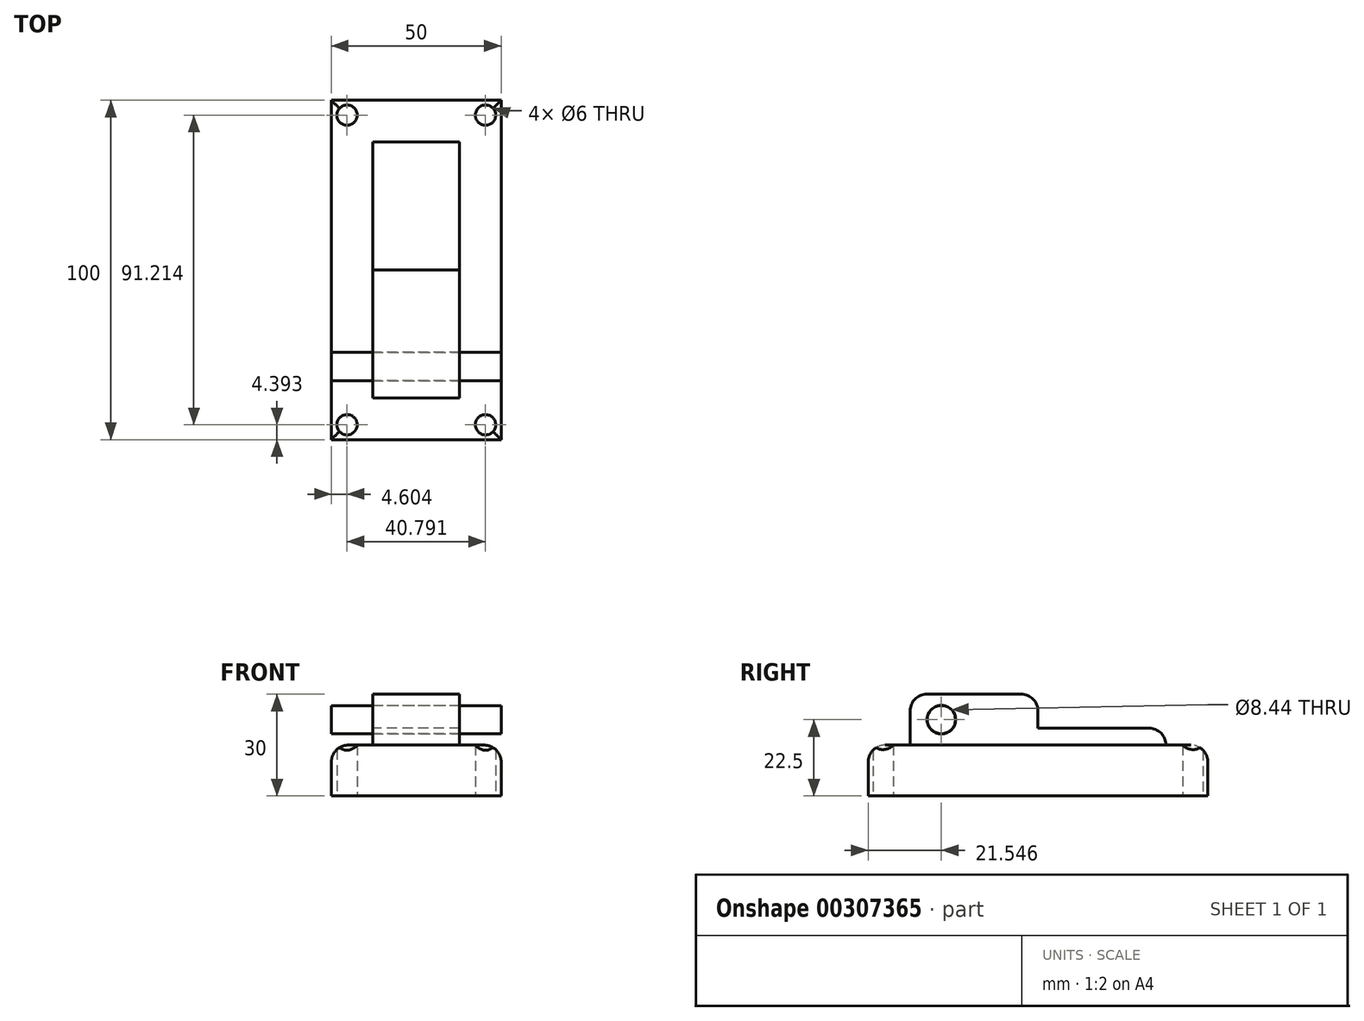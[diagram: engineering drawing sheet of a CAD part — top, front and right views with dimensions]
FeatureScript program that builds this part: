
annotation { "Feature Type Name" : "Feature", "Feature Type Description" : "" }
export const myFeature = defineFeature(function(context is Context, id is Id, definition is map)
    precondition{}
    {
        {
            var Q0;
            Q0=qCreatedBy(makeId("Top.planeOp"),FACE);
            var sketch = newSketch(context, id + "F0", { "sketchPlane" : qUnion([Q0])});
            skLineSegment(sketch, "E0.bottom", {"start": v(25, 50) * mm, "end": v(-25, 50) * mm});
            skLineSegment(sketch, "E0.top", {"start": v(25, -50) * mm, "end": v(-25, -50) * mm});
            skLineSegment(sketch, "E0.left", {"start": v(25, 50) * mm, "end": v(25, -50) * mm});
            skLineSegment(sketch, "E0.right", {"start": v(-25, 50) * mm, "end": v(-25, -50) * mm});
            skPoint(sketch, "E0.middle", {"position": v(0, 0) * mm});
            skLineSegment(sketch, "E1.bottom", {"start": v(20.4, 45.6) * mm, "end": v(-20.4, 45.6) * mm, "construction": true});
            skLineSegment(sketch, "E1.top", {"start": v(20.4, -45.6) * mm, "end": v(-20.4, -45.6) * mm, "construction": true});
            skLineSegment(sketch, "E1.left", {"start": v(20.4, 45.6) * mm, "end": v(20.4, -45.6) * mm, "construction": true});
            skLineSegment(sketch, "E1.right", {"start": v(-20.4, 45.6) * mm, "end": v(-20.4, -45.6) * mm, "construction": true});
            skCircle(sketch, "E2", {"center": v(-20.4, 45.6) * mm, "radius": 3 * mm});
            skCircle(sketch, "E3", {"center": v(20.4, 45.6) * mm, "radius": 3 * mm});
            skCircle(sketch, "E4", {"center": v(-20.4, -45.6) * mm, "radius": 3 * mm});
            skCircle(sketch, "E5", {"center": v(20.4, -45.6) * mm, "radius": 3 * mm});
            skLineSegment(sketch, "E6.bottom", {"start": v(12.75, 37.68) * mm, "end": v(-12.75, 37.68) * mm});
            skLineSegment(sketch, "E6.top", {"start": v(12.75, -37.68) * mm, "end": v(-12.75, -37.68) * mm});
            skLineSegment(sketch, "E6.left", {"start": v(12.75, 37.68) * mm, "end": v(12.75, -37.68) * mm});
            skLineSegment(sketch, "E6.right", {"start": v(-12.75, 37.68) * mm, "end": v(-12.75, -37.68) * mm});
            skLineSegment(sketch, "E7.top", {"start": v(12.75, 0) * mm, "end": v(-12.75, 0) * mm});
            skLineSegment(sketch, "E7.left", {"start": v(12.75, 37.68) * mm, "end": v(12.75, 0) * mm});
            skLineSegment(sketch, "E7.right", {"start": v(-12.75, 37.68) * mm, "end": v(-12.75, 0) * mm});
            skSolve(sketch);
        }
        {
            var Q0;
            Q0=makeQuery(id+"F0.imprint","IMPRINT",FACE,{"disambiguationData":[TD([[makeQuery(id+"F0.imprint","IMPRINT",EDGE,{"derivedFrom":sQuery(id+"F0.wireOp",EDGE,"E0.bottom")}),1.0]])]});
            extrude(context, id + "F1", {"entities" : qUnion([Q0]), "depth" : 15 * mm});
        }
        {
            var Q0;
            Q0=makeQuery(id+"F0.imprint","IMPRINT",FACE,{"disambiguationData":[TD([[makeQuery(id+"F0.imprint","IMPRINT",EDGE,{"derivedFrom":sQuery(id+"F0.wireOp",EDGE,"E6.bottom")}),1.0]])]});
            extrude(context, id + "F2", {"entities" : qUnion([Q0]), "operationType" : NewBodyOperationType.ADD, "depth" : 20 * mm});
        }
        {
            var Q0;
            Q0=makeQuery(id+"F0.imprint","IMPRINT",FACE,{"disambiguationData":[TD([[makeQuery(id+"F0.imprint","IMPRINT",EDGE,{"derivedFrom":sQuery(id+"F0.wireOp",EDGE,"E6.top")}),-1.0]])]});
            extrude(context, id + "F3", {"entities" : qUnion([Q0]), "operationType" : NewBodyOperationType.ADD, "depth" : 30 * mm});
        }
        {
            var Q0;
            Q0=makeQuery(id+"F3.opExtrude","CAP_EDGE",EDGE,{"disambiguationData":[OSD([sQuery(id+"F0.wireOp",EDGE,"E7.top")])],"isStart":false});
            var Q1;
            Q1=makeQuery(id+"F2.opExtrude","CAP_EDGE",EDGE,{"disambiguationData":[OSD([sQuery(id+"F0.wireOp",EDGE,"E7.top")])],"isStart":false});
            var Q2;
            Q2=makeQuery(id+"F2.opExtrude","CAP_EDGE",EDGE,{"disambiguationData":[OSD([sQuery(id+"F0.wireOp",EDGE,"E6.bottom")])],"isStart":false});
            var Q3;
            Q3=makeQuery(id+"F1.opExtrude","CAP_EDGE",EDGE,{"disambiguationData":[OSD([sQuery(id+"F0.wireOp",EDGE,"E0.right")])],"isStart":false});
            var Q4;
            Q4=makeQuery(id+"F1.opExtrude","CAP_EDGE",EDGE,{"disambiguationData":[OSD([sQuery(id+"F0.wireOp",EDGE,"E0.top")])],"isStart":false});
            var Q5;
            Q5=makeQuery(id+"F1.opExtrude","CAP_EDGE",EDGE,{"disambiguationData":[OSD([sQuery(id+"F0.wireOp",EDGE,"E0.left")])],"isStart":false});
            var Q6;
            Q6=makeQuery(id+"F1.opExtrude","CAP_EDGE",EDGE,{"disambiguationData":[OSD([sQuery(id+"F0.wireOp",EDGE,"E0.bottom")])],"isStart":false});
            var Q7;
            Q7=makeQuery(id+"F3.opExtrude","CAP_EDGE",EDGE,{"disambiguationData":[OSD([sQuery(id+"F0.wireOp",EDGE,"E6.top")])],"isStart":false});
            var Q8;
            Q8=makeQuery(id+"F1.opExtrude","CAP_EDGE",EDGE,{"disambiguationData":[OSD([sQuery(id+"F0.wireOp",EDGE,"E6.top")])],"isStart":false});
            fillet(context, id + "F4", {"entities" : qUnion([Q0, Q1, Q2, Q3, Q4, Q5, Q6, Q7, Q8]), "radius" : 5 * mm, "tangentPropagation" : true, "allowEdgeOverflow" : false});
        }
        {
            var Q0;
            Q0=makeQuery(id+"F3.boolean.opBoolean","MERGE",FACE,{"derivedFrom":[makeQuery(id+"F2.opExtrude","SWEPT_FACE",FACE,{"disambiguationData":[OSD([sQuery(id+"F0.wireOp",EDGE,"E7.left")])]}),makeQuery(id+"F3.opExtrude","SWEPT_FACE",FACE,{"disambiguationData":[OSD([sQuery(id+"F0.wireOp",EDGE,"E6.left")])]})]});
            var sketch = newSketch(context, id + "F5", { "sketchPlane" : qUnion([Q0])});
            skLineSegment(sketch, "E8.bottom", {"start": v(-37.68, 15) * mm, "end": v(-5, 15) * mm, "construction": true});
            skLineSegment(sketch, "E8.top", {"start": v(-37.68, 30) * mm, "end": v(-5, 30) * mm, "construction": true});
            skLineSegment(sketch, "E8.left", {"start": v(-37.68, 15) * mm, "end": v(-37.68, 30) * mm, "construction": true});
            skLineSegment(sketch, "E8.right", {"start": v(-5, 15) * mm, "end": v(-5, 30) * mm, "construction": true});
            skLineSegment(sketch, "E9.bottom", {"start": v(-32.68, 30) * mm, "end": v(-24.23, 30) * mm, "construction": true});
            skLineSegment(sketch, "E9.top", {"start": v(-32.68, 15) * mm, "end": v(-24.23, 15) * mm, "construction": true});
            skLineSegment(sketch, "E9.left", {"start": v(-32.68, 30) * mm, "end": v(-32.68, 15) * mm, "construction": true});
            skLineSegment(sketch, "E9.right", {"start": v(-24.23, 30) * mm, "end": v(-24.23, 15) * mm, "construction": true});
            skLineSegment(sketch, "E10", {"start": v(-32.68, 22.5) * mm, "end": v(-24.23, 22.5) * mm, "construction": true});
            skCircle(sketch, "E11", {"center": v(-28.45, 22.5) * mm, "radius": 4.22 * mm});
            skSolve(sketch);
        }
        {
            var Q0;
            Q0 = qSketchRegion(id + "F5", true);
            extrude(context, id + "F6", {"entities" : qUnion([Q0]), "operationType" : NewBodyOperationType.REMOVE, "oppositeDirection" : true, "depth" : 31.6 * mm});
        }
        {
            var Q0;
            Q0=qCreatedBy(makeId("Right.planeOp"),FACE);
            var sketch = newSketch(context, id + "F7", { "sketchPlane" : qUnion([Q0])});
            skCircle(sketch, "E12", {"center": v(-28.45, 22.5) * mm, "radius": 4.15 * mm});
            skSolve(sketch);
        }
        {
            var Q0;
            Q0=makeQuery(id+"F7.imprint","IMPRINT",FACE,{"disambiguationData":[TD([[makeQuery(id+"F7.imprint","IMPRINT",EDGE,{"derivedFrom":sQuery(id+"F7.wireOp",EDGE,"E12")}),1.0]])]});
            extrude(context, id + "F8", {"entities" : qUnion([Q0]), "endBound" : BoundingType.SYMMETRIC, "depth" : 50 * mm});
        }
    });
